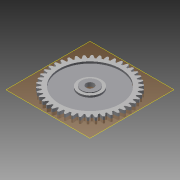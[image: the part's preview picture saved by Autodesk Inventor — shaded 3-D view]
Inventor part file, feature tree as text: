
AUTODESK INVENTOR PART (.ipt)
format: ipt  version: 2014 (Build 180170000, 170)  size: 379,392 bytes
history: native  units: mm
features: other x5, extrude x2, sketch x2, mirror x1
ambient origin geometry x8: Origin, YZ Plane, XZ Plane, XY Plane, X Axis, Y Axis, Z Axis, Center Point
bodies: Body1 (feature_tree)
feature tree (10):
  other  "平歯車2"
  extrude  "押し出し1"  Depth=10.0mm
  extrude  "押し出し2"  Depth=5.2mm
  other  "作業平面1"
  mirror  "ミラー1"
  other  "Solid1::平歯車2"
  other  "TaggingFeature1"
  sketch  "スケッチ1"
  sketch  "スケッチ2"
  other  "ソリッド1"
